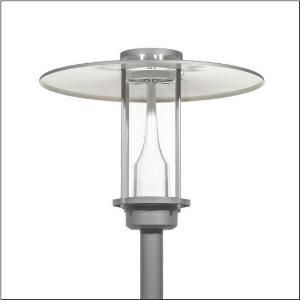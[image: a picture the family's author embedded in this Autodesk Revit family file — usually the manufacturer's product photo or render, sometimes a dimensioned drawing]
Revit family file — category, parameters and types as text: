
# Revit family: city-light_plus_iq___st1_2a_5xa5275mf14hp_2b63
name_source: partatom
category: Lighting Fixtures
units: mm (PartAtom-declared; Revit-internal decimal feet)

## family parameters
Cut with Voids When Loaded = No
Host = Face
Light Source = No
Part Type = Normal
Room Calculation Point = No
Round Connector Dimension = Use Diameter
Shared = No

## types (1)
- --- (1 x LED, 4040 lm, 33.6 W, 2700K)
    Apparent Load = 34 VA
    CIE Flux Codes = 22 60 93 97 100
    Color Rendering = 70
    Color Temperature = 2700K
    Default Elevation = 1800 mm
    Description = City-Light Plus iQ, mast luminaire, Module 540 iQ-SR, primary light control with 3 zone facetted reflector, of plastic, silver coated, highly specular, structured, primary optical cover: cover, of PMMA, transparent, light distribution: ST1.2a, light emission: direct distribution, primary light characteristic: asymmetric, installation type: post-top, LED, High Power LED, rated luminous flux: 4.040lm, luminous efficacy: 120lm/W, light colour: 727, colour temperature: 2700K, control gear: ECG iQ, control: presetting dimming logarithmic, Street-Remote, Auto-Match, Temp-Guard, Lumen-Switch, Night-Set, Smart-Wire, Light-Fading, Desk-Remote (wireless, voltage-free reading and setting of iQ features in the workshop via application-optimized NFC function/RFID function), optimised constant luminous flux control (CLO 2.0), with terminal, 6-pole, max. 2.5mm², mains connection: 230..240V, AC, 50/60Hz, start of lifetime: 34W, end of service life: 36W, reduction: 15W, luminaire housing, upper part, of glass-fibre reinforced polyester, coated, Siteco® metallic grey (DB 702S), diameter: 750mm, height: 590mm, spigot size: d x l = 76 x 70mm (post-top) | with reducer (optional accessory) 60 x 70mm, post-top mast mounting element, of diecast aluminium, coated, Siteco® metallic grey (DB 702S), Module 540 iQ-SR, traffic white (RAL 9016), equipment: Power, protection rating (complete): IP65, insulation class (complete): insulation class II (safety insulation), certification: CE, ENEC, VDE, packaging unit: 1 piece

Light Distribution: ST1.2a
    Height = 590 mm
    Lamp = 1 x LED
    Lamp Light Flux = 4040 lm
    Lamp Power = 33.6 W
    Lamp count = 1
    Length = 750 mm
    Luminous efficacy = 120 lm/W
    Manufacturer = Siteco
    ModVariant = No
    Model = 5XA5275MF14HP
    Number of Poles = 1
    OnlyDefault = Yes
    Power Factor = 1
    Product Name = City-Light Plus iQ | ST1.2a
    Product group = mast luminaire | pylon top
    ProductGroupID = 6100
    Protection Class = Protection class II
    Protection Degree = IP 65
    RLX_Detail_Level = 1
    RLX_Emergency_Light_Flux = 0 lm
    RLX_Emergency_Type = 0
    RLX_Emergency_Type_DB = No
    RlxData = <blob elided: 52473 chars, md5=9121d79e>
    Socket = socket
    Standby Power = 0 W
    System Light Flux = 4040 lm
    System Power = 34 W
    Type Comments = factory setting: luminous flux: 100 % | dim-lin: 254 | 695 mA
    Type Image = l_1006456.jpg
    URL = http://relux.com
    VarID = @adj_103001
    Voltage = 0 V
    Weight = 0.00 kg
    Width = 0 mm  [stored 0 ft]

note: [stored X ft] marks values corroborated as IEEE doubles in the binary element streams (Revit-internal decimal feet)

## geometry (parser evidence)
native form markers: Blend x4, Sweep x13
no freeform markers — native parametric forms only
